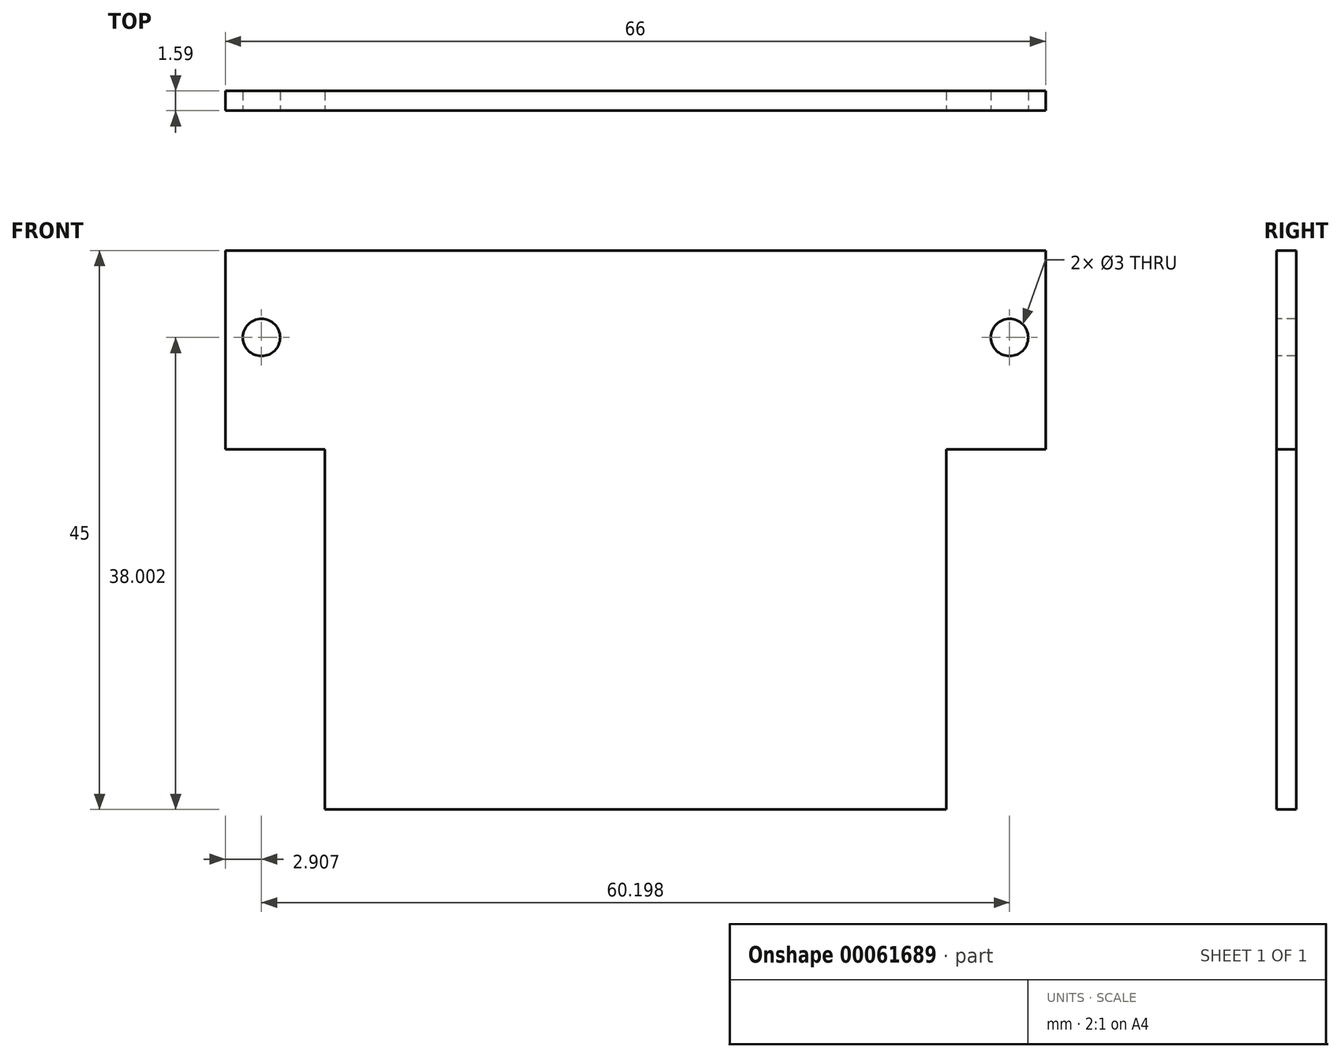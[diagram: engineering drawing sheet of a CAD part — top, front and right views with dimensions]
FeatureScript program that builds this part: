
annotation { "Feature Type Name" : "Feature", "Feature Type Description" : "" }
export const myFeature = defineFeature(function(context is Context, id is Id, definition is map)
    precondition{}
    {
        {
            var Q0;
            Q0=qCreatedBy(makeId("Front.planeOp"),FACE);
            var sketch = newSketch(context, id + "F0", { "sketchPlane" : qUnion([Q0])});
            skLineSegment(sketch, "E0.bottom", {"start": v(-27.66, 21.16) * mm, "end": v(40.34, 21.16) * mm});
            skLineSegment(sketch, "E0.top", {"start": v(-27.66, -23.84) * mm, "end": v(40.34, -23.84) * mm});
            skLineSegment(sketch, "E0.left", {"start": v(-27.66, 21.16) * mm, "end": v(-27.66, -23.84) * mm});
            skLineSegment(sketch, "E0.right", {"start": v(40.34, 21.16) * mm, "end": v(40.34, -23.84) * mm});
            skSolve(sketch);
        }
        {
            var Q0;
            Q0=makeQuery(id+"F0.imprint","IMPRINT",FACE,{"disambiguationData":[TD([[makeQuery(id+"F0.imprint","IMPRINT",EDGE,{"derivedFrom":sQuery(id+"F0.wireOp",EDGE,"E0.bottom")}),-1.0]])]});
            extrude(context, id + "F1", {"entities" : qUnion([Q0]), "depth" : 1.59 * mm});
        }
        {
            var Q0;
            Q0=makeQuery(id+"F1.opExtrude","CAP_FACE",FACE,{"disambiguationData":[OSD([sQuery(id+"F0.wireOp",EDGE,"E0.bottom"),sQuery(id+"F0.wireOp",EDGE,"E0.top"),sQuery(id+"F0.wireOp",EDGE,"E0.left"),sQuery(id+"F0.wireOp",EDGE,"E0.right")])],"isStart":false});
            var sketch = newSketch(context, id + "F2", { "sketchPlane" : qUnion([Q0])});
            skLineSegment(sketch, "E1.bottom", {"start": v(-27.66, -23.84) * mm, "end": v(-18.66, -23.84) * mm});
            skLineSegment(sketch, "E1.top", {"start": v(-27.66, 5.16) * mm, "end": v(-18.66, 5.16) * mm});
            skLineSegment(sketch, "E1.left", {"start": v(-27.66, -23.84) * mm, "end": v(-27.66, 5.16) * mm});
            skLineSegment(sketch, "E1.right", {"start": v(-18.66, -23.84) * mm, "end": v(-18.66, 5.16) * mm});
            skLineSegment(sketch, "E2.bottom", {"start": v(40.34, -23.84) * mm, "end": v(31.34, -23.84) * mm});
            skLineSegment(sketch, "E2.top", {"start": v(40.34, 5.16) * mm, "end": v(31.34, 5.16) * mm});
            skLineSegment(sketch, "E2.left", {"start": v(40.34, -23.84) * mm, "end": v(40.34, 5.16) * mm});
            skLineSegment(sketch, "E2.right", {"start": v(31.34, -23.84) * mm, "end": v(31.34, 5.16) * mm});
            skCircle(sketch, "E3", {"center": v(-23.75, 14.16) * mm, "radius": 1.63 * mm});
            skCircle(sketch, "E4", {"center": v(36.44, 14.16) * mm, "radius": 2.04 * mm});
            skSolve(sketch);
        }
        {
            var Q0;
            Q0=makeQuery(id+"F2.imprint","IMPRINT",FACE,{"disambiguationData":[TD([[makeQuery(id+"F2.imprint","IMPRINT",EDGE,{"derivedFrom":sQuery(id+"F2.wireOp",EDGE,"E1.bottom")}),1.0]])]});
            var Q1;
            Q1=makeQuery(id+"F2.imprint","IMPRINT",FACE,{"disambiguationData":[TD([[makeQuery(id+"F2.imprint","IMPRINT",EDGE,{"derivedFrom":sQuery(id+"F2.wireOp",EDGE,"E2.bottom")}),1.0]])]});
            extrude(context, id + "F3", {"entities" : qUnion([Q0, Q1]), "operationType" : NewBodyOperationType.REMOVE, "oppositeDirection" : true, "depth" : 25.4 * mm});
        }
        {
            var Q0;
            Q0=sQuery(id+"F2.wireOp",VERTEX,"E3.center");
            var Q1;
            Q1=sQuery(id+"F2.wireOp",VERTEX,"E4.center");
            var Q2;
            Q2=makeQuery(id+"F1.opExtrude","SWEPT_BODY",BODY,{"disambiguationData":[OSD([sQuery(id+"F0.wireOp",EDGE,"E0.bottom"),sQuery(id+"F0.wireOp",EDGE,"E0.top"),sQuery(id+"F0.wireOp",EDGE,"E0.left"),sQuery(id+"F0.wireOp",EDGE,"E0.right")])]});
            hole(context, id + "F4", {"style" : HoleStyle.SIMPLE, "holeDiameter" : 3 * mm, "endStyle" : HoleEndStyle.THROUGH, "locations" : qUnion([Q0, Q1]), "scope" : qUnion([Q2])});
        }
        {
            var Q0;
            Q0=makeQuery(id+"F1.opExtrude","CAP_FACE",FACE,{"disambiguationData":[OSD([sQuery(id+"F0.wireOp",EDGE,"E0.bottom"),sQuery(id+"F0.wireOp",EDGE,"E0.top"),sQuery(id+"F0.wireOp",EDGE,"E0.left"),sQuery(id+"F0.wireOp",EDGE,"E0.right")])],"isStart":false});
            var sketch = newSketch(context, id + "F5", { "sketchPlane" : qUnion([Q0])});
            skLineSegment(sketch, "E5.bottom", {"start": v(-27.66, 21.16) * mm, "end": v(-26.66, 21.16) * mm});
            skLineSegment(sketch, "E5.top", {"start": v(-27.66, 5.16) * mm, "end": v(-26.66, 5.16) * mm});
            skLineSegment(sketch, "E5.left", {"start": v(-27.66, 21.16) * mm, "end": v(-27.66, 5.16) * mm});
            skLineSegment(sketch, "E5.right", {"start": v(-26.66, 21.16) * mm, "end": v(-26.66, 5.16) * mm});
            skLineSegment(sketch, "E6.bottom", {"start": v(40.34, 21.16) * mm, "end": v(39.34, 21.16) * mm});
            skLineSegment(sketch, "E6.top", {"start": v(40.34, 5.16) * mm, "end": v(39.34, 5.16) * mm});
            skLineSegment(sketch, "E6.left", {"start": v(40.34, 21.16) * mm, "end": v(40.34, 5.16) * mm});
            skLineSegment(sketch, "E6.right", {"start": v(39.34, 21.16) * mm, "end": v(39.34, 5.16) * mm});
            skSolve(sketch);
        }
        {
            var Q0;
            Q0 = qSketchRegion(id + "F5", true);
            extrude(context, id + "F6", {"entities" : qUnion([Q0]), "operationType" : NewBodyOperationType.REMOVE, "oppositeDirection" : true, "depth" : 25.4 * mm});
        }
    });
